# Revit family: Magnuson-Slide-Wall_Mounted_Coat_Tree-1
name_source: partatom
category: Furniture
revit_build: Autodesk Revit 2016 (Build: 20150220_1215(x64)
units: mm (PartAtom-declared; Revit-internal decimal feet)

## family parameters
Cut with Voids When Loaded = No
Host = Face
Room Calculation Point = No
Shared = No

## types (1)
- SLIDE W2
    Assembly Code = E2020200
    Base Finish = MAG-Paint Steel White
    Cap Finish = MAG-Paint Steel White
    Default Elevation = 48"
    Depth = 7 3/4"
    Description = Wall mounted coat tree with 5 hooks
    Height = 50"
    Hook Finish = MAG-Plastic White
    Keynote = 12500
    Low Emitting Finish = Yes
    Low Emitting Material = Yes
    Manufacturer = Magnuson Group
    Model = SLIDE W2
    Percentage of Recycled Content = 0
    Post Finish = MAG-Paint Steel White
    Revit File Built By = https://servex-us.com
    Salvage or Reuse = No
    Type Comments = Coat Hook Strips
    URL = www.magnusongroup.com
    Width = 4 11/16"

## geometry (parser evidence)
native form markers: Sweep x6
no freeform markers — native parametric forms only
